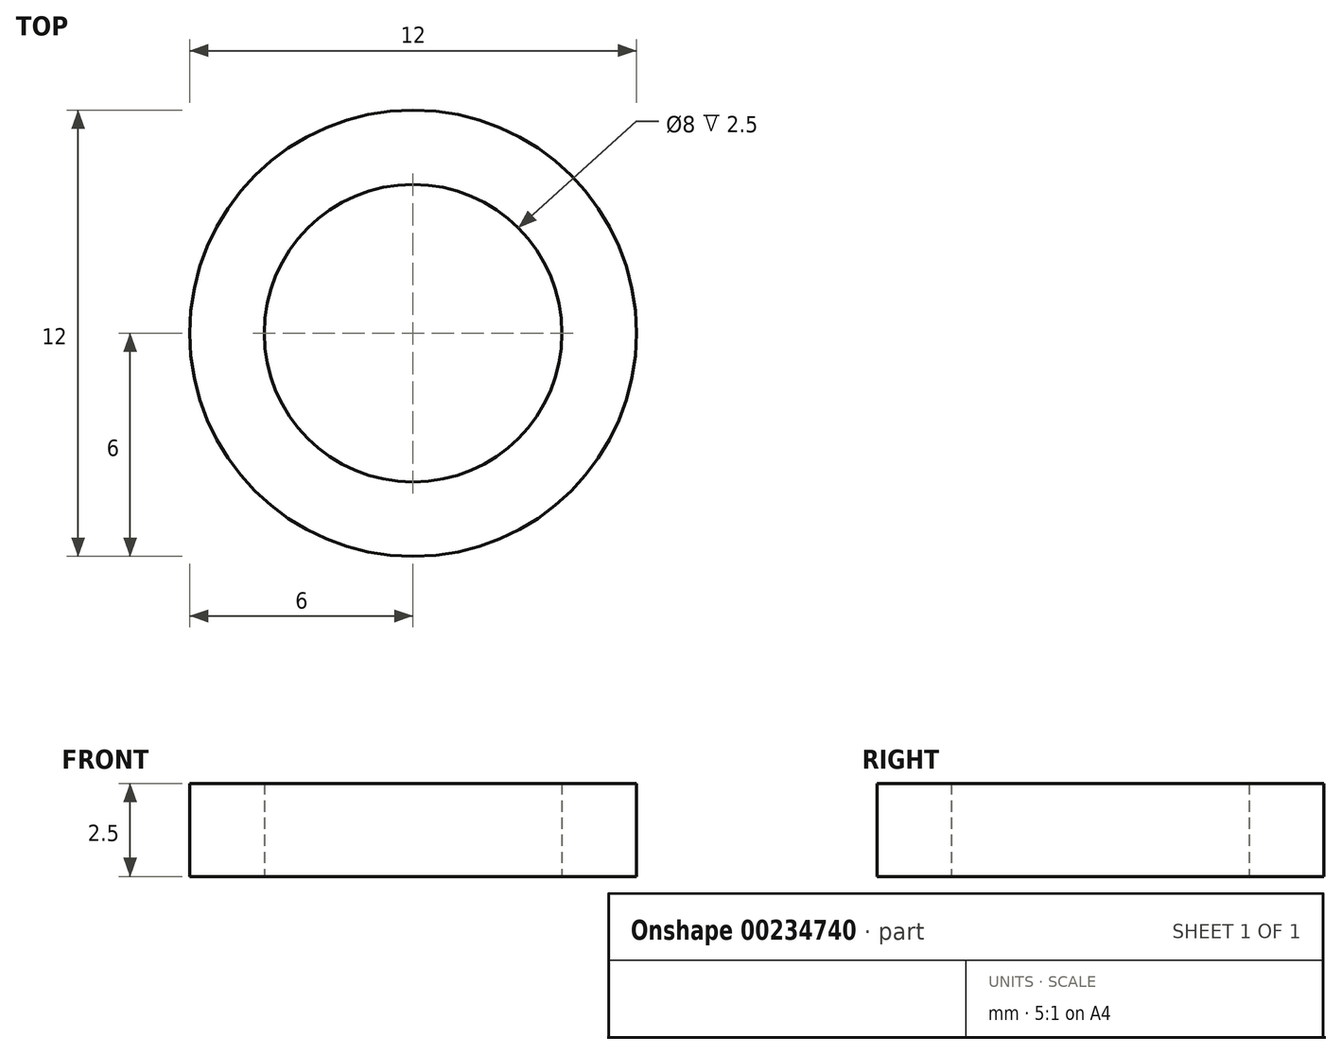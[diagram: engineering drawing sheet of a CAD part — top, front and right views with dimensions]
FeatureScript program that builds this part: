
annotation { "Feature Type Name" : "Feature", "Feature Type Description" : "" }
export const myFeature = defineFeature(function(context is Context, id is Id, definition is map)
    precondition{}
    {
        {
            var Q0;
            Q0=qCreatedBy(makeId("Top.planeOp"),FACE);
            var sketch = newSketch(context, id + "F0", { "sketchPlane" : qUnion([Q0])});
            skCircle(sketch, "E0", {"center": v(0, 0) * mm, "radius": 6 * mm});
            skCircle(sketch, "E1", {"center": v(0, 0) * mm, "radius": 4 * mm});
            skSolve(sketch);
        }
        {
            var Q0;
            Q0=qSketchRegion(id+"F0",true);
            extrude(context, id + "F1", {"entities" : qUnion([Q0]), "endBound" : BoundingType.SYMMETRIC, "depth" : 2.5 * mm});
        }
    });
